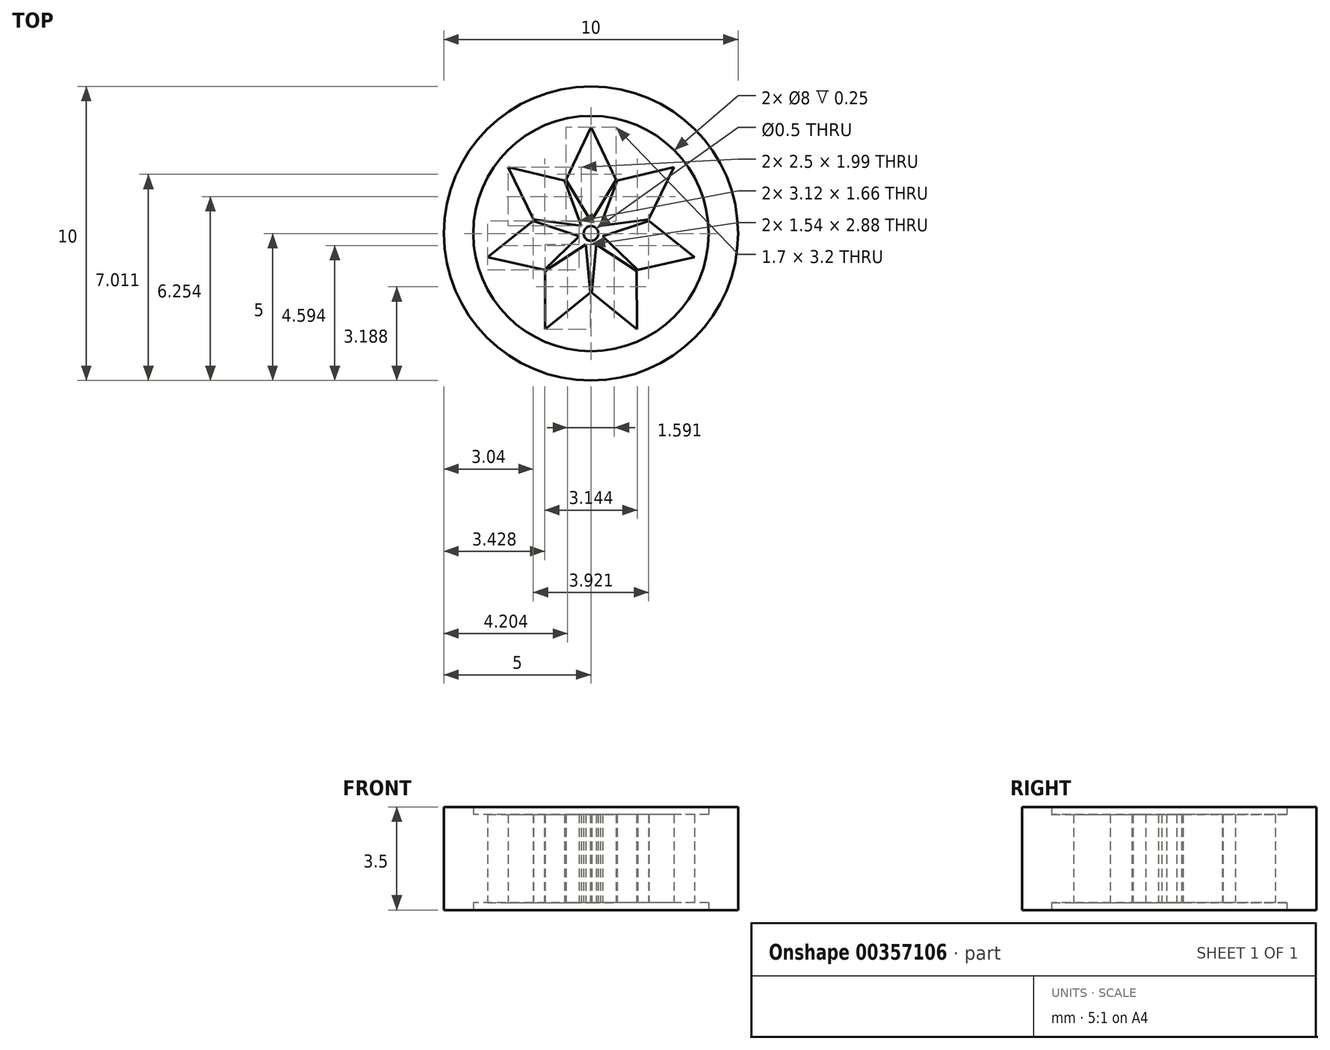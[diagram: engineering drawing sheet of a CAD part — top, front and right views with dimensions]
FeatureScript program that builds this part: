
annotation { "Feature Type Name" : "Feature", "Feature Type Description" : "" }
export const myFeature = defineFeature(function(context is Context, id is Id, definition is map)
    precondition{}
    {
        {
            var Q0;
            Q0=qCreatedBy(makeId("Top.planeOp"),FACE);
            var sketch = newSketch(context, id + "F0", { "sketchPlane" : qUnion([Q0])});
            skCircle(sketch, "E0", {"center": v(0, 0) * mm, "radius": 0.25 * mm});
            skCircle(sketch, "E1", {"center": v(0, 0) * mm, "radius": 4 * mm});
            skCircle(sketch, "E2", {"center": v(0, 0) * mm, "radius": 5 * mm});
            skLineSegment(sketch, "E3", {"start": v(0, 3.6) * mm, "end": v(-0.85, 1.82) * mm});
            skLineSegment(sketch, "E4", {"start": v(-0.85, 1.82) * mm, "end": v(0, 0.41) * mm});
            skLineSegment(sketch, "E5.MirrorCS", {"start": v(0, 3.6) * mm, "end": v(0.85, 1.82) * mm});
            skLineSegment(sketch, "E6.MirrorCS", {"start": v(0.85, 1.82) * mm, "end": v(0, 0.41) * mm});
            skLineSegment(sketch, "E7.1.1", {"start": v(-0.9, 1.8) * mm, "end": v(-0.32, 0.26) * mm});
            skLineSegment(sketch, "E7.1.2", {"start": v(-2.82, 2.25) * mm, "end": v(-0.9, 1.8) * mm});
            skLineSegment(sketch, "E7.1.3", {"start": v(-1.96, 0.47) * mm, "end": v(-0.32, 0.26) * mm});
            skLineSegment(sketch, "E7.1.4", {"start": v(-2.82, 2.25) * mm, "end": v(-1.96, 0.47) * mm});
            skLineSegment(sketch, "E7.2.1", {"start": v(-1.97, 0.42) * mm, "end": v(-0.4, -0.1) * mm});
            skLineSegment(sketch, "E7.2.2", {"start": v(-3.52, -0.8) * mm, "end": v(-1.97, 0.42) * mm});
            skLineSegment(sketch, "E7.2.3", {"start": v(-1.59, -1.23) * mm, "end": v(-0.4, -0.1) * mm});
            skLineSegment(sketch, "E7.2.4", {"start": v(-3.52, -0.8) * mm, "end": v(-1.59, -1.23) * mm});
            skLineSegment(sketch, "E7.3.1", {"start": v(-1.56, -1.27) * mm, "end": v(-0.18, -0.37) * mm});
            skLineSegment(sketch, "E7.3.2", {"start": v(-1.57, -3.25) * mm, "end": v(-1.56, -1.27) * mm});
            skLineSegment(sketch, "E7.3.3", {"start": v(-0.03, -2.01) * mm, "end": v(-0.18, -0.37) * mm});
            skLineSegment(sketch, "E7.3.4", {"start": v(-1.57, -3.25) * mm, "end": v(-0.03, -2.01) * mm});
            skLineSegment(sketch, "E7.4.1", {"start": v(0.03, -2.01) * mm, "end": v(0.18, -0.37) * mm});
            skLineSegment(sketch, "E7.4.2", {"start": v(1.57, -3.25) * mm, "end": v(0.03, -2.01) * mm});
            skLineSegment(sketch, "E7.4.3", {"start": v(1.56, -1.27) * mm, "end": v(0.18, -0.37) * mm});
            skLineSegment(sketch, "E7.4.4", {"start": v(1.57, -3.25) * mm, "end": v(1.56, -1.27) * mm});
            skLineSegment(sketch, "E7.5.1", {"start": v(1.59, -1.23) * mm, "end": v(0.4, -0.1) * mm});
            skLineSegment(sketch, "E7.5.2", {"start": v(3.52, -0.8) * mm, "end": v(1.59, -1.23) * mm});
            skLineSegment(sketch, "E7.5.3", {"start": v(1.97, 0.42) * mm, "end": v(0.4, -0.1) * mm});
            skLineSegment(sketch, "E7.5.4", {"start": v(3.52, -0.8) * mm, "end": v(1.97, 0.42) * mm});
            skLineSegment(sketch, "E7.6.1", {"start": v(1.96, 0.47) * mm, "end": v(0.32, 0.26) * mm});
            skLineSegment(sketch, "E7.6.2", {"start": v(2.82, 2.25) * mm, "end": v(1.96, 0.47) * mm});
            skLineSegment(sketch, "E7.6.3", {"start": v(0.9, 1.8) * mm, "end": v(0.32, 0.26) * mm});
            skLineSegment(sketch, "E7.6.4", {"start": v(2.82, 2.25) * mm, "end": v(0.9, 1.8) * mm});
            skSolve(sketch);
        }
        {
            var Q0;
            Q0=makeQuery(id+"F0.imprint","IMPRINT",FACE,{"disambiguationData":[TD([[makeQuery(id+"F0.imprint","IMPRINT",EDGE,{"derivedFrom":sQuery(id+"F0.wireOp",EDGE,"E0")}),-1.0]])]});
            extrude(context, id + "F1", {"entities" : qUnion([Q0]), "endBound" : BoundingType.SYMMETRIC, "depth" : 3 * mm});
        }
        {
            var Q0;
            Q0 = qSketchRegion(id + "F0", true);
            extrude(context, id + "F2", {"entities" : qUnion([Q0]), "operationType" : NewBodyOperationType.ADD, "endBound" : BoundingType.SYMMETRIC, "depth" : 3.5 * mm});
        }
    });
